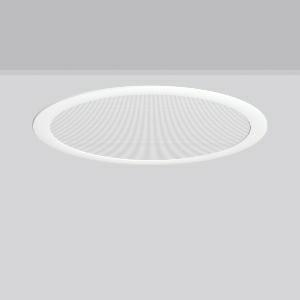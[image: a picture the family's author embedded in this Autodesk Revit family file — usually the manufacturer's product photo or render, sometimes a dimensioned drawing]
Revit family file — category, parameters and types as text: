
# Revit family: toledo_flat_round_e_672379_002_5431
name_source: partatom
category: Lighting Fixtures
units: mm (PartAtom-declared; Revit-internal decimal feet)

## family parameters
Cut with Voids When Loaded = No
Host = Face
Light Source = No
Part Type = Normal
Room Calculation Point = No
Round Connector Dimension = Use Diameter
Shared = No

## types (1)
- TOLEDO FLAT round E (1 x LED Modul 830, 3450 lm, 3000)
    Apparent Load = 30 VA
    CIE Flux Codes = 62 86 96 100 100
    Color Rendering = 80
    Color Temperature = 3000
    Default Elevation = 1800 mm
    Description = Series: TOLEDO FLAT round
Ultra thin recessed downlight. For escape route illumination. Housing: die-cast aluminium, powder-coated. Lightguide and diffuser made of non-yellowing PMMA, prismatic. Ceiling installation with spring system. Including separate LED converter with connecting cable 250 mm. Suitable for connection to central battery systems. External driver with simple plug-in locking system. 
Colour: white
Diameter: 495 mm
Height: 6 mm
Cut-out diameter: 470 mm
Recess height: 40 mm
Luminaire: recess height: 31-51 mm
Weight: 2.6 kg
Operating mode: maintained power mode
Lamp: LED
Socket: without socket
Colour temperature: 3000K
Colour rendering index (CRI): 80
System power: 30 W
Rated luminous flux: 3450 lm
Luminous flux, emergency: 3450 lm
System power, emergency: 30 W
Control gear: Regulated power supply
Protection class: II
Type of protection: IP 54
    Height = 0 mm  [stored 0 ft]
    Lamp = 1 x LED Modul 830
    Lamp Light Flux = 3450 lm
    Lamp count = 1
    Length = 495 mm
    Lifetime = 50000 h
    Luminous efficacy = 115 lm/W
    Manufacturer = RZB
    ModVariant = No
    Model = 672379.002
    Mounting Place = Ceiling
    Mounting Type = Recessed
    Number of Poles = 1
    OnlyDefault = Yes
    Power Factor = 1
    Product Name = TOLEDO FLAT round E
    Product group = Recessed downlights
    ProductGroupID = 402
    Protection Class = Protection class II
    Protection Degree = IP 20
    RLX_Detail_Level = 1
    RLX_Emergency_Light_Flux = 3450 lm
    RLX_Emergency_Type = 3
    RLX_Emergency_Type_DB = Yes
    RlxData = <blob elided: 38857 chars, md5=bc39b2b2>
    Socket = socket
    Standby Power = 0 W
    System Light Flux = 3450 lm
    System Power = 30 W
    Type Comments = Product without accessories
    Type Image = 901586.002.jpg
    URL = http://relux.com
    VarID = ---
    Voltage = 230 V
    Voltage Range = 220-240 V
    Weight = 0.00 kg
    Width = 0 mm  [stored 0 ft]

note: [stored X ft] marks values corroborated as IEEE doubles in the binary element streams (Revit-internal decimal feet)

## geometry (parser evidence)
native form markers: Blend x4, Sweep x11
no freeform markers — native parametric forms only
